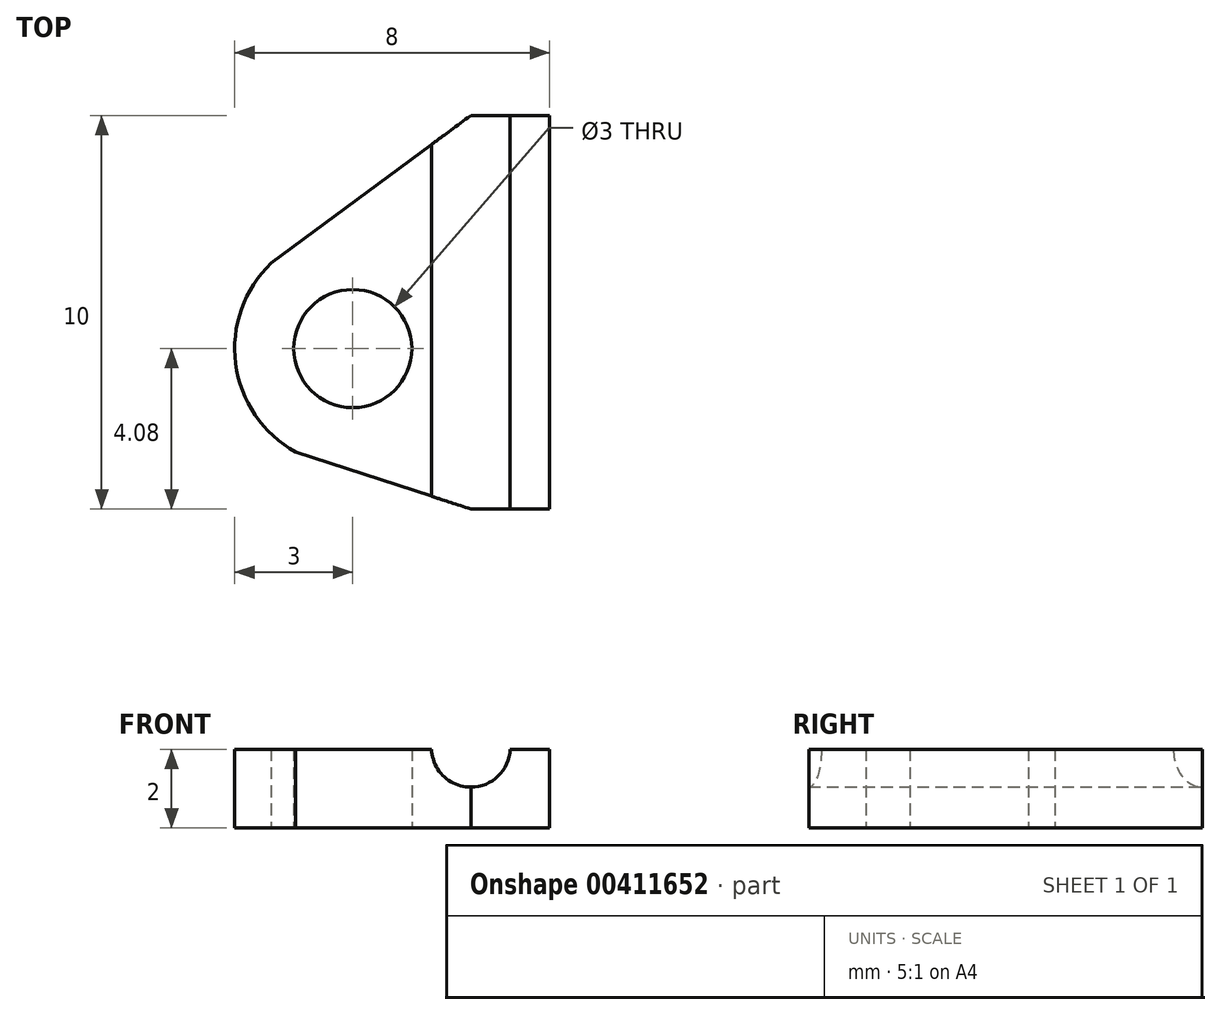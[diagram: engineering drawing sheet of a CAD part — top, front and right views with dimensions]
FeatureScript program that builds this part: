
annotation { "Feature Type Name" : "Feature", "Feature Type Description" : "" }
export const myFeature = defineFeature(function(context is Context, id is Id, definition is map)
    precondition{}
    {
        {
            var Q0;
            Q0=qCreatedBy(makeId("Top.planeOp"),FACE);
            var sketch = newSketch(context, id + "F0", { "sketchPlane" : qUnion([Q0])});
            skCircle(sketch, "E0", {"center": v(0, 0) * mm, "radius": 1.5 * mm});
            skArc(sketch, "E1", {"start": v(-2.07, 2.17) * mm, "mid": v(-2.98, -0.38) * mm, "end": v(-1.45, -2.63) * mm});
            skLineSegment(sketch, "E2", {"start": v(3, 5.92) * mm, "end": v(5, 5.92) * mm});
            skLineSegment(sketch, "E3", {"start": v(5, 5.92) * mm, "end": v(5, -4.08) * mm});
            skLineSegment(sketch, "E4", {"start": v(5, -4.08) * mm, "end": v(3, -4.08) * mm});
            skLineSegment(sketch, "E5", {"start": v(3, 5.92) * mm, "end": v(-2.07, 2.17) * mm});
            skLineSegment(sketch, "E6", {"start": v(3, -4.08) * mm, "end": v(-1.45, -2.63) * mm});
            skSolve(sketch);
        }
        {
            var Q0;
            Q0=makeQuery(id+"F0.imprint","IMPRINT",FACE,{"disambiguationData":[TD([[makeQuery(id+"F0.imprint","IMPRINT",EDGE,{"derivedFrom":sQuery(id+"F0.wireOp",EDGE,"E0")}),-1.0]])]});
            extrude(context, id + "F1", {"entities" : qUnion([Q0]), "depth" : 2 * mm});
        }
        {
            var Q0;
            Q0=makeQuery(id+"F1.opExtrude","SWEPT_FACE",FACE,{"disambiguationData":[OSD([sQuery(id+"F0.wireOp",EDGE,"E2")])]});
            var sketch = newSketch(context, id + "F2", { "sketchPlane" : qUnion([Q0])});
            skPoint(sketch, "E7.startSnap0", {"position": v(-5, 1) * mm});
            skPoint(sketch, "E8.startSnap0", {"position": v(-4, 0) * mm});
            skArc(sketch, "E9", {"start": v(-4, 2) * mm, "mid": v(-2.96, 1.04) * mm, "end": v(-2, 2.08) * mm});
            skLineSegment(sketch, "E10", {"start": v(-2, 2.08) * mm, "end": v(-4, 2) * mm});
            skSolve(sketch);
        }
        {
            var Q0;
            {var subQ0=sQuery(id+"F2.wireOp",EDGE,"E9");var subQ1=sQuery(id+"F0.wireOp",EDGE,"E2");var subQ2=makeQuery(id+"F1.opExtrude","CAP_EDGE",EDGE,{"disambiguationData":[OSD([subQ1])],"isStart":false});var subQ3=makeQuery(id+"F2.imprint","INTERSECT",VERTEX,{"derivedFrom":[subQ2,subQ0,sQuery(id+"F2.wireOp",EDGE,"E10")]});Q0=makeQuery(id+"F2.imprint","IMPRINT",FACE,{"disambiguationData":[TD([[makeQuery(id+"F2.imprint","IMPRINT",EDGE,{"disambiguationData":[TD([[subQ3,-1.0]])],"derivedFrom":subQ0}),1.0]])]});}
            var Q1;
            {var subQ0=sQuery(id+"F2.wireOp",EDGE,"E10");Q1=makeQuery(id+"F2.imprint","IMPRINT",FACE,{"disambiguationData":[TD([[makeQuery(id+"F2.imprint","IMPRINT",EDGE,{"derivedFrom":subQ0}),1.0]])]});}
            extrude(context, id + "F3", {"entities" : qUnion([Q0, Q1]), "operationType" : NewBodyOperationType.REMOVE, "oppositeDirection" : true, "depth" : 25 * mm});
        }
    });
